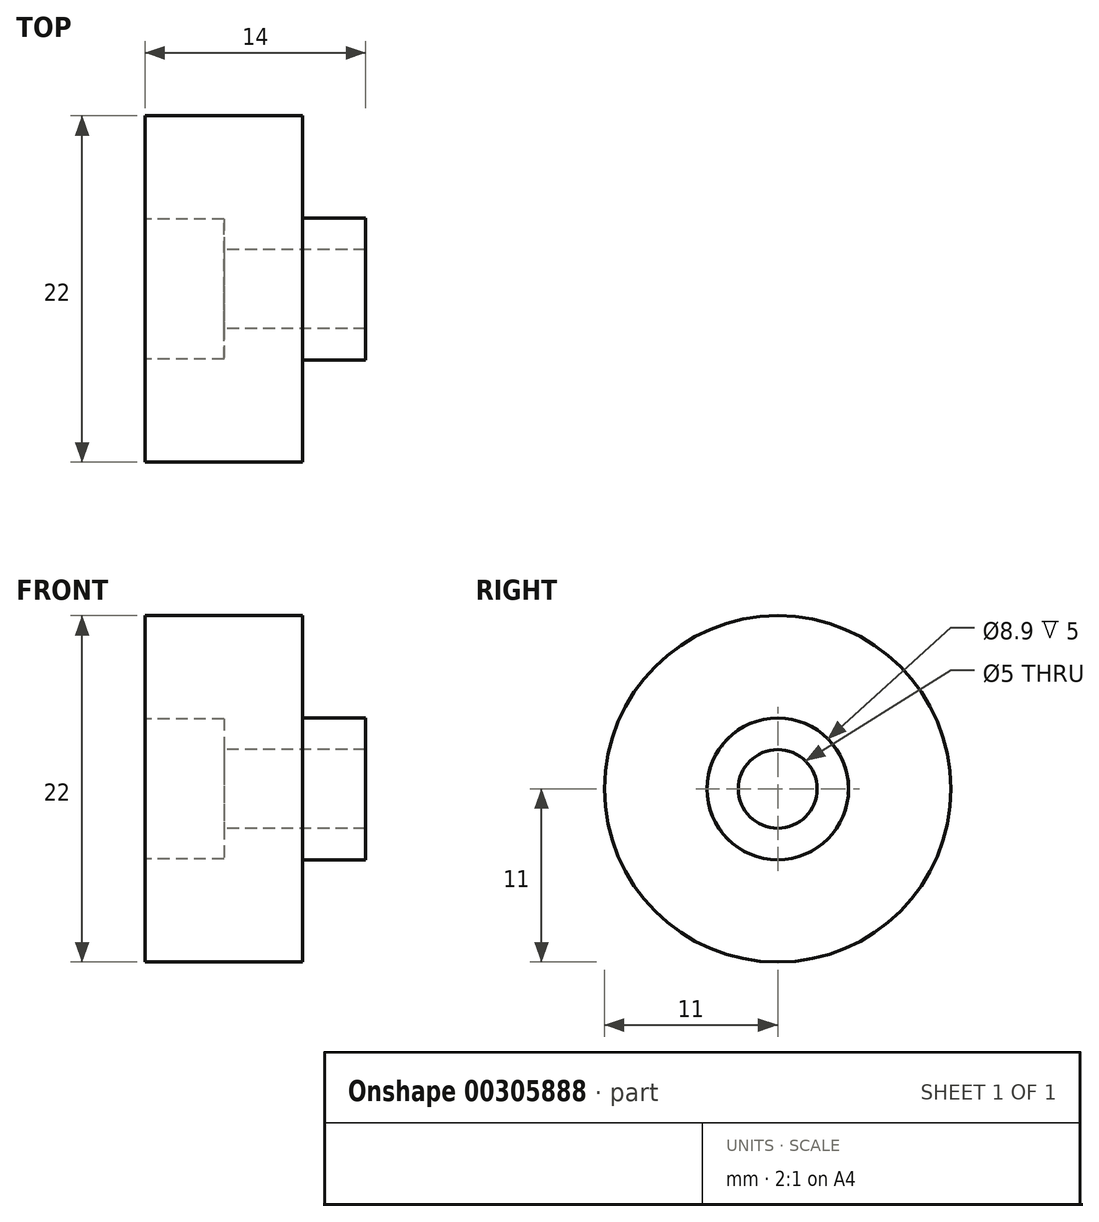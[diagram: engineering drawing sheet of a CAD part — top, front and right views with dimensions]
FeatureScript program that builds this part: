
annotation { "Feature Type Name" : "Feature", "Feature Type Description" : "" }
export const myFeature = defineFeature(function(context is Context, id is Id, definition is map)
    precondition{}
    {
        {
            var Q0;
            Q0=qCreatedBy(makeId("Front.planeOp"),FACE);
            var sketch = newSketch(context, id + "F0", { "sketchPlane" : qUnion([Q0])});
            skLineSegment(sketch, "E0", {"start": v(0, 11) * mm, "end": v(10, 11) * mm});
            skLineSegment(sketch, "E1", {"start": v(10, 11) * mm, "end": v(10, 4.5) * mm});
            skLineSegment(sketch, "E2", {"start": v(10, 4.5) * mm, "end": v(14, 4.5) * mm});
            skLineSegment(sketch, "E3", {"start": v(14, 4.5) * mm, "end": v(14, 2.5) * mm});
            skLineSegment(sketch, "E4", {"start": v(14, 2.5) * mm, "end": v(5, 2.5) * mm});
            skLineSegment(sketch, "E5", {"start": v(5, 2.5) * mm, "end": v(5, 4.45) * mm});
            skLineSegment(sketch, "E6", {"start": v(5, 4.45) * mm, "end": v(0, 4.45) * mm});
            skLineSegment(sketch, "E7", {"start": v(0, 4.45) * mm, "end": v(0, 11) * mm});
            skLineSegment(sketch, "E8", {"start": v(0, 0) * mm, "end": v(24.66, 0) * mm, "construction": true});
            skSolve(sketch);
        }
        {
            var Q0;
            Q0=makeQuery(id+"F0.imprint","IMPRINT",FACE,{"disambiguationData":[TD([[makeQuery(id+"F0.imprint","IMPRINT",EDGE,{"derivedFrom":sQuery(id+"F0.wireOp",EDGE,"E0")}),-1.0]])]});
            var Q1;
            Q1=sQuery(id+"F0.wireOp",EDGE,"E8");
            revolve(context, id + "F1", {"entities" : qUnion([Q0]), "axis" : qUnion([Q1]), "revolveType" : RevolveType.FULL});
        }
    });
